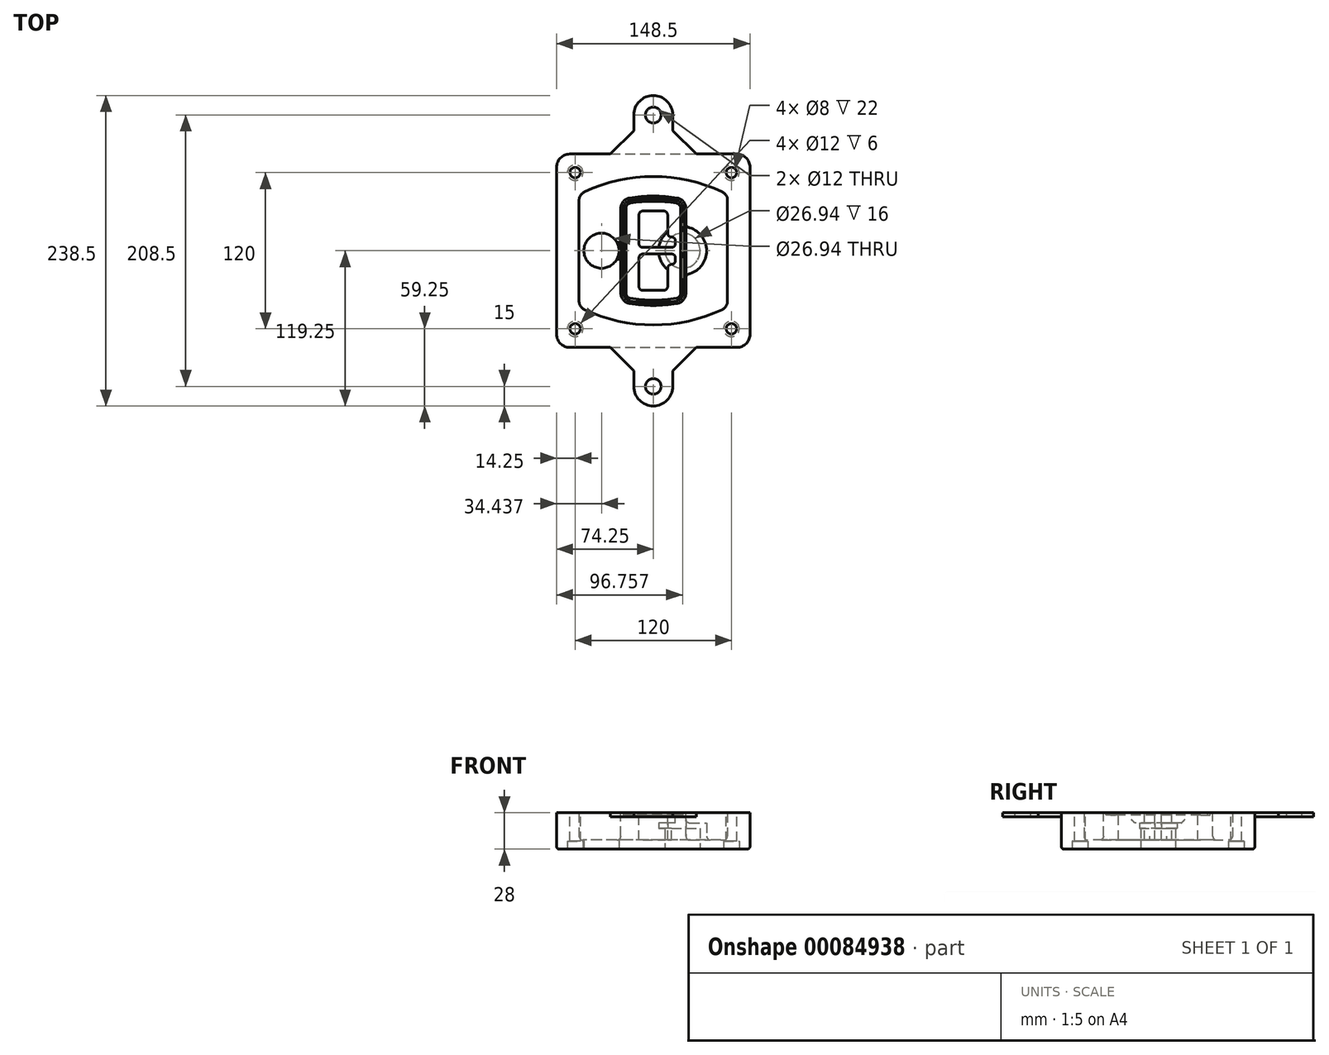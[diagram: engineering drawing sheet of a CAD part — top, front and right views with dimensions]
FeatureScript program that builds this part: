
annotation { "Feature Type Name" : "Feature", "Feature Type Description" : "" }
export const myFeature = defineFeature(function(context is Context, id is Id, definition is map)
    precondition{}
    {
        {
            var Q0;
            Q0=qCreatedBy(makeId("Top.planeOp"),FACE);
            var sketch = newSketch(context, id + "F0", { "sketchPlane" : qUnion([Q0])});
            skPoint(sketch, "E0.rect.middle", {"position": v(0, 0) * mm});
            skLineSegment(sketch, "E1.bottom", {"start": v(-64.25, -74.25) * mm, "end": v(64.25, -74.25) * mm});
            skLineSegment(sketch, "E1.top", {"start": v(-64.25, 74.25) * mm, "end": v(64.25, 74.25) * mm});
            skLineSegment(sketch, "E1.left", {"start": v(-74.25, -64.25) * mm, "end": v(-74.25, 64.25) * mm});
            skLineSegment(sketch, "E1.right", {"start": v(74.25, -64.25) * mm, "end": v(74.25, 64.25) * mm});
            skLineSegment(sketch, "E2", {"start": v(-74.25, 74.25) * mm, "end": v(74.25, -74.25) * mm, "construction": true});
            skLineSegment(sketch, "E3", {"start": v(74.25, 74.25) * mm, "end": v(-74.25, -74.25) * mm, "construction": true});
            skCircle(sketch, "E4", {"center": v(-60, 60) * mm, "radius": 4 * mm});
            skCircle(sketch, "E5", {"center": v(60, 60) * mm, "radius": 4 * mm});
            skCircle(sketch, "E6", {"center": v(60, -60) * mm, "radius": 4 * mm});
            skCircle(sketch, "E7", {"center": v(-60, -60) * mm, "radius": 4 * mm});
            skLineSegment(sketch, "E8", {"start": v(-60, 60) * mm, "end": v(60, 60) * mm, "construction": true});
            skLineSegment(sketch, "E9", {"start": v(60, 60) * mm, "end": v(60, -60) * mm, "construction": true});
            skLineSegment(sketch, "E10", {"start": v(60, -60) * mm, "end": v(-60, -60) * mm, "construction": true});
            skLineSegment(sketch, "E11", {"start": v(-60, -60) * mm, "end": v(-60, 60) * mm, "construction": true});
            skLineSegment(sketch, "E12", {"start": v(-60, 38.83) * mm, "end": v(-60, -38.83) * mm});
            skLineSegment(sketch, "E13", {"start": v(60, 38.83) * mm, "end": v(60, -38.83) * mm});
            skArc(sketch, "E14", {"start": v(54.26, 47.88) * mm, "mid": v(0, 60) * mm, "end": v(-54.26, 47.88) * mm});
            skArc(sketch, "E15", {"start": v(-54.26, -47.88) * mm, "mid": v(0, -60) * mm, "end": v(54.26, -47.88) * mm});
            skLineSegment(sketch, "E16", {"start": v(-60, 0) * mm, "end": v(60, 0) * mm, "construction": true});
            skPoint(sketch, "E17.visualSharp", {"position": v(-60, -45) * mm});
            skArc(sketch, "E17.filletArc", {"start": v(-60, -38.83) * mm, "mid": v(-58.44, -44.2) * mm, "end": v(-54.26, -47.88) * mm});
            skPoint(sketch, "E18.visualSharp", {"position": v(-60, 45) * mm});
            skArc(sketch, "E18.filletArc", {"start": v(-54.26, 47.88) * mm, "mid": v(-58.44, 44.2) * mm, "end": v(-60, 38.83) * mm});
            skPoint(sketch, "E19.visualSharp", {"position": v(60, 45) * mm});
            skArc(sketch, "E19.filletArc", {"start": v(60, 38.83) * mm, "mid": v(58.44, 44.2) * mm, "end": v(54.26, 47.88) * mm});
            skPoint(sketch, "E20.visualSharp", {"position": v(60, -45) * mm});
            skArc(sketch, "E20.filletArc", {"start": v(54.26, -47.88) * mm, "mid": v(58.44, -44.2) * mm, "end": v(60, -38.83) * mm});
            skPoint(sketch, "E21.visualSharp", {"position": v(-74.25, 74.25) * mm});
            skArc(sketch, "E21.filletArc", {"start": v(-64.25, 74.25) * mm, "mid": v(-71.32, 71.32) * mm, "end": v(-74.25, 64.25) * mm});
            skPoint(sketch, "E22.visualSharp", {"position": v(74.25, 74.25) * mm});
            skArc(sketch, "E22.filletArc", {"start": v(74.25, 64.25) * mm, "mid": v(71.32, 71.32) * mm, "end": v(64.25, 74.25) * mm});
            skPoint(sketch, "E23.visualSharp", {"position": v(74.25, -74.25) * mm});
            skArc(sketch, "E23.filletArc", {"start": v(64.25, -74.25) * mm, "mid": v(71.32, -71.32) * mm, "end": v(74.25, -64.25) * mm});
            skPoint(sketch, "E24.visualSharp", {"position": v(-74.25, -74.25) * mm});
            skArc(sketch, "E24.filletArc", {"start": v(-74.25, -64.25) * mm, "mid": v(-71.32, -71.32) * mm, "end": v(-64.25, -74.25) * mm});
            skArc(sketch, "E25.0", {"start": v(57, 38.83) * mm, "mid": v(55.9, 42.58) * mm, "end": v(52.98, 45.17) * mm});
            skLineSegment(sketch, "E25.1", {"start": v(57, 38.83) * mm, "end": v(57, -38.83) * mm});
            skArc(sketch, "E25.2", {"start": v(52.98, -45.17) * mm, "mid": v(55.9, -42.58) * mm, "end": v(57, -38.83) * mm});
            skArc(sketch, "E25.3", {"start": v(-52.98, -45.17) * mm, "mid": v(0, -57) * mm, "end": v(52.98, -45.17) * mm});
            skArc(sketch, "E25.4", {"start": v(-57, -38.83) * mm, "mid": v(-55.9, -42.58) * mm, "end": v(-52.98, -45.17) * mm});
            skArc(sketch, "E25.5", {"start": v(52.98, 45.17) * mm, "mid": v(0, 57) * mm, "end": v(-52.98, 45.17) * mm});
            skLineSegment(sketch, "E25.6", {"start": v(-57, 38.83) * mm, "end": v(-57, -38.83) * mm});
            skArc(sketch, "E25.7", {"start": v(-52.98, 45.17) * mm, "mid": v(-55.9, 42.58) * mm, "end": v(-57, 38.83) * mm});
            skArc(sketch, "E26.0", {"start": v(-55.96, 51.5) * mm, "mid": v(-61.82, 46.33) * mm, "end": v(-64, 38.83) * mm});
            skArc(sketch, "E26.1", {"start": v(55.96, 51.5) * mm, "mid": v(0, 64) * mm, "end": v(-55.96, 51.5) * mm});
            skArc(sketch, "E26.2", {"start": v(64, 38.83) * mm, "mid": v(61.82, 46.33) * mm, "end": v(55.96, 51.5) * mm});
            skLineSegment(sketch, "E26.3", {"start": v(64, 38.83) * mm, "end": v(64, -38.83) * mm});
            skArc(sketch, "E26.4", {"start": v(55.96, -51.5) * mm, "mid": v(61.82, -46.33) * mm, "end": v(64, -38.83) * mm});
            skLineSegment(sketch, "E26.5", {"start": v(-64, 38.83) * mm, "end": v(-64, -38.83) * mm});
            skArc(sketch, "E26.6", {"start": v(-55.96, -51.5) * mm, "mid": v(0, -64) * mm, "end": v(55.96, -51.5) * mm});
            skArc(sketch, "E26.7", {"start": v(-64, -38.83) * mm, "mid": v(-61.82, -46.33) * mm, "end": v(-55.96, -51.5) * mm});
            skSolve(sketch);
        }
        {
            var Q0;
            Q0=makeQuery(id+"F0.imprint","IMPRINT",FACE,{"disambiguationData":[TD([[makeQuery(id+"F0.imprint","IMPRINT",EDGE,{"derivedFrom":sQuery(id+"F0.wireOp",EDGE,"E1.bottom")}),1.0]])]});
            var Q1;
            Q1=makeQuery(id+"F0.imprint","IMPRINT",FACE,{"disambiguationData":[TD([[makeQuery(id+"F0.imprint","IMPRINT",EDGE,{"derivedFrom":sQuery(id+"F0.wireOp",EDGE,"E12")}),1.0]])]});
            var Q2;
            Q2=makeQuery(id+"F0.imprint","IMPRINT",FACE,{"disambiguationData":[TD([[makeQuery(id+"F0.imprint","IMPRINT",EDGE,{"derivedFrom":sQuery(id+"F0.wireOp",EDGE,"E25.0")}),1.0]])]});
            var Q3;
            Q3=makeQuery(id+"F0.imprint","IMPRINT",FACE,{"disambiguationData":[TD([[makeQuery(id+"F0.imprint","IMPRINT",EDGE,{"derivedFrom":sQuery(id+"F0.wireOp",EDGE,"E12")}),-1.0]])]});
            extrude(context, id + "F1", {"entities" : qUnion([Q0, Q1, Q2, Q3]), "oppositeDirection" : true, "depth" : 25 * mm});
        }
        {
            var Q0;
            Q0=makeQuery(id+"F0.imprint","IMPRINT",FACE,{"disambiguationData":[TD([[makeQuery(id+"F0.imprint","IMPRINT",EDGE,{"derivedFrom":sQuery(id+"F0.wireOp",EDGE,"E12")}),1.0]])]});
            extrude(context, id + "F2", {"entities" : qUnion([Q0]), "operationType" : NewBodyOperationType.ADD, "depth" : 3 * mm});
        }
        {
            var Q0;
            Q0=makeQuery(id+"F0.imprint","IMPRINT",FACE,{"disambiguationData":[TD([[makeQuery(id+"F0.imprint","IMPRINT",EDGE,{"derivedFrom":sQuery(id+"F0.wireOp",EDGE,"E25.0")}),1.0]])]});
            extrude(context, id + "F3", {"entities" : qUnion([Q0]), "operationType" : NewBodyOperationType.REMOVE, "oppositeDirection" : true, "depth" : 18 * mm});
        }
        {
            var Q0;
            Q0=makeQuery(id+"F2.opExtrude","CAP_FACE",FACE,{"disambiguationData":[OSD([sQuery(id+"F0.wireOp",EDGE,"E12"),sQuery(id+"F0.wireOp",EDGE,"E13"),sQuery(id+"F0.wireOp",EDGE,"E14"),sQuery(id+"F0.wireOp",EDGE,"E15"),sQuery(id+"F0.wireOp",EDGE,"E17.filletArc"),sQuery(id+"F0.wireOp",EDGE,"E18.filletArc"),sQuery(id+"F0.wireOp",EDGE,"E19.filletArc"),sQuery(id+"F0.wireOp",EDGE,"E20.filletArc"),sQuery(id+"F0.wireOp",EDGE,"E25.0"),sQuery(id+"F0.wireOp",EDGE,"E25.1"),sQuery(id+"F0.wireOp",EDGE,"E25.2"),sQuery(id+"F0.wireOp",EDGE,"E25.3"),sQuery(id+"F0.wireOp",EDGE,"E25.4"),sQuery(id+"F0.wireOp",EDGE,"E25.5"),sQuery(id+"F0.wireOp",EDGE,"E25.6"),sQuery(id+"F0.wireOp",EDGE,"E25.7")])],"isStart":false});
            var sketch = newSketch(context, id + "F4", { "sketchPlane" : qUnion([Q0])});
            skArc(sketch, "E27.0", {"start": v(-18.34, -40.45) * mm, "mid": v(0, -42) * mm, "end": v(18.34, -40.45) * mm});
            skArc(sketch, "E28.0", {"start": v(18.34, 40.45) * mm, "mid": v(0, 42) * mm, "end": v(-18.34, 40.45) * mm});
            skLineSegment(sketch, "E29", {"start": v(-25, 32.57) * mm, "end": v(-25, -32.57) * mm});
            skLineSegment(sketch, "E30", {"start": v(25, 32.57) * mm, "end": v(25, -32.57) * mm});
            skLineSegment(sketch, "E31", {"start": v(-25, 39.1) * mm, "end": v(25, 39.1) * mm, "construction": true});
            skLineSegment(sketch, "E32", {"start": v(-25, -39.1) * mm, "end": v(25, -39.1) * mm, "construction": true});
            skPoint(sketch, "E33.visualSharp", {"position": v(-25, 39.1) * mm});
            skArc(sketch, "E33.filletArc", {"start": v(-18.34, 40.45) * mm, "mid": v(-23.11, 37.73) * mm, "end": v(-25, 32.57) * mm});
            skPoint(sketch, "E34.visualSharp", {"position": v(25, 39.1) * mm});
            skArc(sketch, "E34.filletArc", {"start": v(25, 32.57) * mm, "mid": v(23.11, 37.73) * mm, "end": v(18.34, 40.45) * mm});
            skPoint(sketch, "E35.visualSharp", {"position": v(25, -39.1) * mm});
            skArc(sketch, "E35.filletArc", {"start": v(18.34, -40.45) * mm, "mid": v(23.11, -37.73) * mm, "end": v(25, -32.57) * mm});
            skPoint(sketch, "E36.visualSharp", {"position": v(-25, -39.1) * mm});
            skArc(sketch, "E36.filletArc", {"start": v(-25, -32.57) * mm, "mid": v(-23.11, -37.73) * mm, "end": v(-18.34, -40.45) * mm});
            skArc(sketch, "E37.0", {"start": v(52.98, 45.17) * mm, "mid": v(0, 57) * mm, "end": v(-52.98, 45.17) * mm});
            skArc(sketch, "E37.1", {"start": v(-52.98, 45.17) * mm, "mid": v(-55.9, 42.58) * mm, "end": v(-57, 38.83) * mm});
            skLineSegment(sketch, "E37.2", {"start": v(-57, 38.83) * mm, "end": v(-57, -38.83) * mm});
            skArc(sketch, "E37.3", {"start": v(-57, -38.83) * mm, "mid": v(-55.9, -42.58) * mm, "end": v(-52.98, -45.17) * mm});
            skArc(sketch, "E37.4", {"start": v(-52.98, -45.17) * mm, "mid": v(0, -57) * mm, "end": v(52.98, -45.17) * mm});
            skArc(sketch, "E37.5", {"start": v(52.98, -45.17) * mm, "mid": v(55.9, -42.58) * mm, "end": v(57, -38.83) * mm});
            skLineSegment(sketch, "E37.6", {"start": v(57, 38.83) * mm, "end": v(57, -38.83) * mm});
            skArc(sketch, "E37.7", {"start": v(57, 38.83) * mm, "mid": v(55.9, 42.58) * mm, "end": v(52.98, 45.17) * mm});
            skLineSegment(sketch, "E38.0", {"start": v(23, 32.57) * mm, "end": v(23, -32.57) * mm});
            skArc(sketch, "E38.1", {"start": v(18, -38.48) * mm, "mid": v(21.58, -36.44) * mm, "end": v(23, -32.57) * mm});
            skArc(sketch, "E38.2", {"start": v(-18, -38.48) * mm, "mid": v(0, -40) * mm, "end": v(18, -38.48) * mm});
            skArc(sketch, "E38.3", {"start": v(-23, -32.57) * mm, "mid": v(-21.58, -36.44) * mm, "end": v(-18, -38.48) * mm});
            skLineSegment(sketch, "E38.4", {"start": v(-23, 32.57) * mm, "end": v(-23, -32.57) * mm});
            skArc(sketch, "E38.5", {"start": v(23, 32.57) * mm, "mid": v(21.58, 36.44) * mm, "end": v(18, 38.48) * mm});
            skArc(sketch, "E38.6", {"start": v(-18, 38.48) * mm, "mid": v(-21.58, 36.44) * mm, "end": v(-23, 32.57) * mm});
            skArc(sketch, "E38.7", {"start": v(18, 38.48) * mm, "mid": v(0, 40) * mm, "end": v(-18, 38.48) * mm});
            skArc(sketch, "E39.0", {"start": v(21, 32.57) * mm, "mid": v(20.06, 35.15) * mm, "end": v(17.67, 36.5) * mm});
            skLineSegment(sketch, "E39.1", {"start": v(21, 32.57) * mm, "end": v(21, -32.57) * mm});
            skArc(sketch, "E39.2", {"start": v(17.67, -36.5) * mm, "mid": v(20.06, -35.15) * mm, "end": v(21, -32.57) * mm});
            skArc(sketch, "E39.3", {"start": v(-17.67, -36.5) * mm, "mid": v(0, -38) * mm, "end": v(17.67, -36.5) * mm});
            skArc(sketch, "E39.4", {"start": v(-21, -32.57) * mm, "mid": v(-20.06, -35.15) * mm, "end": v(-17.67, -36.5) * mm});
            skArc(sketch, "E39.5", {"start": v(17.67, 36.5) * mm, "mid": v(0, 38) * mm, "end": v(-17.67, 36.5) * mm});
            skLineSegment(sketch, "E39.6", {"start": v(-21, 32.57) * mm, "end": v(-21, -32.57) * mm});
            skArc(sketch, "E39.7", {"start": v(-17.67, 36.5) * mm, "mid": v(-20.06, 35.15) * mm, "end": v(-21, 32.57) * mm});
            skLineSegment(sketch, "E40", {"start": v(-25, 0) * mm, "end": v(25, 0) * mm, "construction": true});
            skLineSegment(sketch, "E41", {"start": v(-11, 5.5) * mm, "end": v(-11, 27.5) * mm});
            skLineSegment(sketch, "E42", {"start": v(-8, 30.5) * mm, "end": v(8, 30.5) * mm});
            skLineSegment(sketch, "E43", {"start": v(11, 27.5) * mm, "end": v(11, 13.5) * mm});
            skLineSegment(sketch, "E44", {"start": v(14, 10.5) * mm, "end": v(14, 10.5) * mm});
            skLineSegment(sketch, "E45", {"start": v(17, 7.5) * mm, "end": v(17, 5.5) * mm});
            skLineSegment(sketch, "E46", {"start": v(14, 2.5) * mm, "end": v(-8, 2.5) * mm});
            skPoint(sketch, "E47.visualSharp", {"position": v(-11, 30.5) * mm});
            skArc(sketch, "E47.filletArc", {"start": v(-8, 30.5) * mm, "mid": v(-10.12, 29.62) * mm, "end": v(-11, 27.5) * mm});
            skPoint(sketch, "E48.visualSharp", {"position": v(11, 30.5) * mm});
            skArc(sketch, "E48.filletArc", {"start": v(11, 27.5) * mm, "mid": v(10.12, 29.62) * mm, "end": v(8, 30.5) * mm});
            skPoint(sketch, "E49.visualSharp", {"position": v(11, 10.5) * mm});
            skArc(sketch, "E49.filletArc", {"start": v(11, 13.5) * mm, "mid": v(11.88, 11.38) * mm, "end": v(14, 10.5) * mm});
            skPoint(sketch, "E50.visualSharp", {"position": v(17, 10.5) * mm});
            skArc(sketch, "E50.filletArc", {"start": v(17, 7.5) * mm, "mid": v(16.12, 9.62) * mm, "end": v(14, 10.5) * mm});
            skPoint(sketch, "E51.visualSharp", {"position": v(17, 2.5) * mm});
            skArc(sketch, "E51.filletArc", {"start": v(14, 2.5) * mm, "mid": v(16.12, 3.38) * mm, "end": v(17, 5.5) * mm});
            skPoint(sketch, "E52.visualSharp", {"position": v(-11, 2.5) * mm});
            skArc(sketch, "E52.filletArc", {"start": v(-11, 5.5) * mm, "mid": v(-10.12, 3.38) * mm, "end": v(-8, 2.5) * mm});
            skLineSegment(sketch, "E53.0.MirrorCS", {"start": v(14, -2.5) * mm, "end": v(-8, -2.5) * mm});
            skArc(sketch, "E54.0.MirrorCS", {"start": v(-11, -5.5) * mm, "mid": v(-10.12, -3.38) * mm, "end": v(-8, -2.5) * mm});
            skLineSegment(sketch, "E55.0.MirrorCS", {"start": v(-11, -5.5) * mm, "end": v(-11, -27.5) * mm});
            skArc(sketch, "E56.0.MirrorCS", {"start": v(-8, -30.5) * mm, "mid": v(-10.12, -29.62) * mm, "end": v(-11, -27.5) * mm});
            skLineSegment(sketch, "E57.0.MirrorCS", {"start": v(-8, -30.5) * mm, "end": v(8, -30.5) * mm});
            skArc(sketch, "E58.0.MirrorCS", {"start": v(11, -27.5) * mm, "mid": v(10.12, -29.62) * mm, "end": v(8, -30.5) * mm});
            skLineSegment(sketch, "E59.0.MirrorCS", {"start": v(11, -27.5) * mm, "end": v(11, -13.5) * mm});
            skArc(sketch, "E60.0.MirrorCS", {"start": v(11, -13.5) * mm, "mid": v(11.88, -11.38) * mm, "end": v(14, -10.5) * mm});
            skArc(sketch, "E61.0.MirrorCS", {"start": v(17, -7.5) * mm, "mid": v(16.12, -9.62) * mm, "end": v(14, -10.5) * mm});
            skLineSegment(sketch, "E62.0.MirrorCS", {"start": v(17, -7.5) * mm, "end": v(17, -5.5) * mm});
            skArc(sketch, "E63.0.MirrorCS", {"start": v(14, -2.5) * mm, "mid": v(16.12, -3.38) * mm, "end": v(17, -5.5) * mm});
            skSolve(sketch);
        }
        {
            var Q0;
            Q0=makeQuery(id+"F4.imprint","IMPRINT",FACE,{"disambiguationData":[TD([[makeQuery(id+"F4.imprint","IMPRINT",EDGE,{"derivedFrom":sQuery(id+"F4.wireOp",EDGE,"E27.0")}),1.0]])]});
            var Q1;
            Q1=makeQuery(id+"F4.imprint","IMPRINT",FACE,{"disambiguationData":[TD([[makeQuery(id+"F4.imprint","IMPRINT",EDGE,{"derivedFrom":sQuery(id+"F4.wireOp",EDGE,"E38.0")}),-1.0]])]});
            var Q2;
            Q2=makeQuery(id+"F4.imprint","IMPRINT",FACE,{"disambiguationData":[TD([[makeQuery(id+"F4.imprint","IMPRINT",EDGE,{"derivedFrom":sQuery(id+"F4.wireOp",EDGE,"E39.0")}),1.0]])]});
            extrude(context, id + "F5", {"entities" : qUnion([Q0, Q1, Q2]), "operationType" : NewBodyOperationType.ADD, "endBound" : BoundingType.UP_TO_NEXT, "oppositeDirection" : true, "depth" : 25 * mm});
        }
        {
            var Q0;
            Q0=makeQuery(id+"F4.imprint","IMPRINT",FACE,{"disambiguationData":[TD([[makeQuery(id+"F4.imprint","IMPRINT",EDGE,{"derivedFrom":sQuery(id+"F4.wireOp",EDGE,"E38.0")}),-1.0]])]});
            extrude(context, id + "F6", {"entities" : qUnion([Q0]), "operationType" : NewBodyOperationType.REMOVE, "oppositeDirection" : true, "depth" : 2 * mm});
        }
        {
            var Q0;
            Q0=makeQuery(id+"F1.opExtrude","CAP_FACE",FACE,{"disambiguationData":[OSD([sQuery(id+"F0.wireOp",EDGE,"E1.bottom"),sQuery(id+"F0.wireOp",EDGE,"E1.top"),sQuery(id+"F0.wireOp",EDGE,"E1.left"),sQuery(id+"F0.wireOp",EDGE,"E1.right"),sQuery(id+"F0.wireOp",EDGE,"E4"),sQuery(id+"F0.wireOp",EDGE,"E5"),sQuery(id+"F0.wireOp",EDGE,"E6"),sQuery(id+"F0.wireOp",EDGE,"E7"),sQuery(id+"F0.wireOp",EDGE,"E21.filletArc"),sQuery(id+"F0.wireOp",EDGE,"E22.filletArc"),sQuery(id+"F0.wireOp",EDGE,"E23.filletArc"),sQuery(id+"F0.wireOp",EDGE,"E24.filletArc")])],"isStart":false});
            var sketch = newSketch(context, id + "F7", { "sketchPlane" : qUnion([Q0])});
            skCircle(sketch, "E64", {"center": v(22.5, 0) * mm, "radius": 13.47 * mm});
            skCircle(sketch, "E65", {"center": v(-39.81, 0) * mm, "radius": 13.47 * mm});
            skLineSegment(sketch, "E66", {"start": v(74.25, 0) * mm, "end": v(-74.25, 0) * mm});
            skCircle(sketch, "E67", {"center": v(22.5, 0) * mm, "radius": 18.47 * mm});
            skCircle(sketch, "E68", {"center": v(60, -60) * mm, "radius": 6 * mm});
            skCircle(sketch, "E69", {"center": v(-60, -60) * mm, "radius": 6 * mm});
            skCircle(sketch, "E70", {"center": v(-60, 60) * mm, "radius": 6 * mm});
            skCircle(sketch, "E71", {"center": v(60, 60) * mm, "radius": 6 * mm});
            skSolve(sketch);
        }
        {
            var Q0;
            {var subQ1=sQuery(id+"F7.wireOp",EDGE,"E66");var subQ4=sQuery(id+"F7.wireOp",EDGE,"E64");var subQ6=makeQuery(id+"F7.imprint","INTERSECT",VERTEX,{"disambiguationData":[OD(0.0)],"derivedFrom":[subQ4,subQ1]});Q0=makeQuery(id+"F7.imprint","IMPRINT",FACE,{"disambiguationData":[TD([[makeQuery(id+"F7.imprint","IMPRINT",EDGE,{"disambiguationData":[TD([[subQ6,-1.0]])],"derivedFrom":subQ4}),-1.0]])]});}
            var Q1;
            {var subQ0=sQuery(id+"F7.wireOp",EDGE,"E66");var subQ1=sQuery(id+"F7.wireOp",EDGE,"E64");var subQ3=makeQuery(id+"F7.imprint","INTERSECT",VERTEX,{"disambiguationData":[OD(0.0)],"derivedFrom":[subQ1,subQ0]});Q1=makeQuery(id+"F7.imprint","IMPRINT",FACE,{"disambiguationData":[TD([[makeQuery(id+"F7.imprint","IMPRINT",EDGE,{"disambiguationData":[TD([[subQ3,-1.0]])],"derivedFrom":subQ1}),1.0]])]});}
            var Q2;
            {var subQ0=sQuery(id+"F7.wireOp",EDGE,"E66");var subQ1=sQuery(id+"F7.wireOp",EDGE,"E64");var subQ3=makeQuery(id+"F7.imprint","INTERSECT",VERTEX,{"disambiguationData":[OD(0.0)],"derivedFrom":[subQ1,subQ0]});Q2=makeQuery(id+"F7.imprint","IMPRINT",FACE,{"disambiguationData":[TD([[makeQuery(id+"F7.imprint","IMPRINT",EDGE,{"disambiguationData":[TD([[subQ3,1.0]])],"derivedFrom":subQ1}),1.0]])]});}
            var Q3;
            {var subQ1=sQuery(id+"F7.wireOp",EDGE,"E66");var subQ4=sQuery(id+"F7.wireOp",EDGE,"E64");var subQ6=makeQuery(id+"F7.imprint","INTERSECT",VERTEX,{"disambiguationData":[OD(0.0)],"derivedFrom":[subQ4,subQ1]});Q3=makeQuery(id+"F7.imprint","IMPRINT",FACE,{"disambiguationData":[TD([[makeQuery(id+"F7.imprint","IMPRINT",EDGE,{"disambiguationData":[TD([[subQ6,1.0]])],"derivedFrom":subQ4}),-1.0]])]});}
            extrude(context, id + "F8", {"entities" : qUnion([Q0, Q1, Q2, Q3]), "operationType" : NewBodyOperationType.ADD, "oppositeDirection" : true, "depth" : 20 * mm});
        }
        {
            var Q0;
            {var subQ0=sQuery(id+"F7.wireOp",EDGE,"E66");var subQ1=sQuery(id+"F7.wireOp",EDGE,"E64");var subQ3=makeQuery(id+"F7.imprint","INTERSECT",VERTEX,{"disambiguationData":[OD(0.0)],"derivedFrom":[subQ1,subQ0]});Q0=makeQuery(id+"F7.imprint","IMPRINT",FACE,{"disambiguationData":[TD([[makeQuery(id+"F7.imprint","IMPRINT",EDGE,{"disambiguationData":[TD([[subQ3,-1.0]])],"derivedFrom":subQ1}),1.0]])]});}
            var Q1;
            {var subQ0=sQuery(id+"F7.wireOp",EDGE,"E66");var subQ1=sQuery(id+"F7.wireOp",EDGE,"E64");var subQ3=makeQuery(id+"F7.imprint","INTERSECT",VERTEX,{"disambiguationData":[OD(0.0)],"derivedFrom":[subQ1,subQ0]});Q1=makeQuery(id+"F7.imprint","IMPRINT",FACE,{"disambiguationData":[TD([[makeQuery(id+"F7.imprint","IMPRINT",EDGE,{"disambiguationData":[TD([[subQ3,1.0]])],"derivedFrom":subQ1}),1.0]])]});}
            extrude(context, id + "F9", {"entities" : qUnion([Q0, Q1]), "operationType" : NewBodyOperationType.REMOVE, "oppositeDirection" : true, "depth" : 16 * mm});
        }
        {
            var Q0;
            {var subQ0=sQuery(id+"F7.wireOp",EDGE,"E66");var subQ1=sQuery(id+"F7.wireOp",EDGE,"E65");var subQ3=makeQuery(id+"F7.imprint","INTERSECT",VERTEX,{"disambiguationData":[OD(0.0)],"derivedFrom":[subQ1,subQ0]});Q0=makeQuery(id+"F7.imprint","IMPRINT",FACE,{"disambiguationData":[TD([[makeQuery(id+"F7.imprint","IMPRINT",EDGE,{"disambiguationData":[TD([[subQ3,-1.0]])],"derivedFrom":subQ1}),1.0]])]});}
            var Q1;
            {var subQ0=sQuery(id+"F7.wireOp",EDGE,"E66");var subQ1=sQuery(id+"F7.wireOp",EDGE,"E65");var subQ3=makeQuery(id+"F7.imprint","INTERSECT",VERTEX,{"disambiguationData":[OD(0.0)],"derivedFrom":[subQ1,subQ0]});Q1=makeQuery(id+"F7.imprint","IMPRINT",FACE,{"disambiguationData":[TD([[makeQuery(id+"F7.imprint","IMPRINT",EDGE,{"disambiguationData":[TD([[subQ3,1.0]])],"derivedFrom":subQ1}),1.0]])]});}
            extrude(context, id + "F10", {"entities" : qUnion([Q0, Q1]), "operationType" : NewBodyOperationType.REMOVE, "oppositeDirection" : true, "depth" : 25 * mm});
        }
        {
            var Q0;
            Q0=makeQuery(id+"F7.imprint","IMPRINT",FACE,{"disambiguationData":[TD([[makeQuery(id+"F7.imprint","IMPRINT",EDGE,{"derivedFrom":sQuery(id+"F7.wireOp",EDGE,"E68")}),1.0]])]});
            var Q1;
            Q1=makeQuery(id+"F7.imprint","IMPRINT",FACE,{"disambiguationData":[TD([[makeQuery(id+"F7.imprint","IMPRINT",EDGE,{"derivedFrom":makeQuery(id+"F1.opExtrude","CAP_EDGE",EDGE,{"disambiguationData":[OSD([sQuery(id+"F0.wireOp",EDGE,"E5")])],"isStart":false})}),-1.0]])]});
            var Q2;
            Q2=makeQuery(id+"F7.imprint","IMPRINT",FACE,{"disambiguationData":[TD([[makeQuery(id+"F7.imprint","IMPRINT",EDGE,{"derivedFrom":sQuery(id+"F7.wireOp",EDGE,"E69")}),1.0]])]});
            var Q3;
            Q3=makeQuery(id+"F7.imprint","IMPRINT",FACE,{"disambiguationData":[TD([[makeQuery(id+"F7.imprint","IMPRINT",EDGE,{"derivedFrom":makeQuery(id+"F1.opExtrude","CAP_EDGE",EDGE,{"disambiguationData":[OSD([sQuery(id+"F0.wireOp",EDGE,"E4")])],"isStart":false})}),-1.0]])]});
            var Q4;
            Q4=makeQuery(id+"F7.imprint","IMPRINT",FACE,{"disambiguationData":[TD([[makeQuery(id+"F7.imprint","IMPRINT",EDGE,{"derivedFrom":sQuery(id+"F7.wireOp",EDGE,"E70")}),1.0]])]});
            var Q5;
            Q5=makeQuery(id+"F7.imprint","IMPRINT",FACE,{"disambiguationData":[TD([[makeQuery(id+"F7.imprint","IMPRINT",EDGE,{"derivedFrom":makeQuery(id+"F1.opExtrude","CAP_EDGE",EDGE,{"disambiguationData":[OSD([sQuery(id+"F0.wireOp",EDGE,"E7")])],"isStart":false})}),-1.0]])]});
            var Q6;
            Q6=makeQuery(id+"F7.imprint","IMPRINT",FACE,{"disambiguationData":[TD([[makeQuery(id+"F7.imprint","IMPRINT",EDGE,{"derivedFrom":sQuery(id+"F7.wireOp",EDGE,"E71")}),1.0]])]});
            var Q7;
            Q7=makeQuery(id+"F7.imprint","IMPRINT",FACE,{"disambiguationData":[TD([[makeQuery(id+"F7.imprint","IMPRINT",EDGE,{"derivedFrom":makeQuery(id+"F1.opExtrude","CAP_EDGE",EDGE,{"disambiguationData":[OSD([sQuery(id+"F0.wireOp",EDGE,"E6")])],"isStart":false})}),-1.0]])]});
            extrude(context, id + "F11", {"entities" : qUnion([Q0, Q1, Q2, Q3, Q4, Q5, Q6, Q7]), "operationType" : NewBodyOperationType.REMOVE, "oppositeDirection" : true, "depth" : 6 * mm});
        }
        {
            var Q0;
            Q0=makeQuery(id+"F9.boolean.opBoolean","COPY",FACE,{"derivedFrom":makeQuery(id+"F9.opExtrude","CAP_FACE",FACE,{"disambiguationData":[OSD([sQuery(id+"F7.wireOp",EDGE,"E64")])],"isStart":false})});
            var sketch = newSketch(context, id + "F12", { "sketchPlane" : qUnion([Q0])});
            skArc(sketch, "E72.0", {"start": v(11, 14.45) * mm, "mid": v(6.45, 9.13) * mm, "end": v(4.2, 2.5) * mm});
            skArc(sketch, "E72.1", {"start": v(4.2, -2.5) * mm, "mid": v(6.45, -9.13) * mm, "end": v(11, -14.45) * mm});
            skLineSegment(sketch, "E73", {"start": v(4.2, -2.5) * mm, "end": v(14, -2.5) * mm});
            skLineSegment(sketch, "E74.0", {"start": v(14, 2.5) * mm, "end": v(4.2, 2.5) * mm});
            skArc(sketch, "E74.1", {"start": v(14, 2.5) * mm, "mid": v(16.12, 3.38) * mm, "end": v(17, 5.5) * mm});
            skLineSegment(sketch, "E74.2", {"start": v(17, 7.5) * mm, "end": v(17, 5.5) * mm});
            skArc(sketch, "E74.3", {"start": v(17, 7.5) * mm, "mid": v(16.12, 9.62) * mm, "end": v(14, 10.5) * mm});
            skArc(sketch, "E74.4", {"start": v(11, 13.5) * mm, "mid": v(11.88, 11.38) * mm, "end": v(14, 10.5) * mm});
            skLineSegment(sketch, "E74.5", {"start": v(11, 14.45) * mm, "end": v(11, 13.5) * mm});
            skLineSegment(sketch, "E74.7", {"start": v(14, -2.5) * mm, "end": v(4.2, -2.5) * mm});
            skArc(sketch, "E74.8", {"start": v(14, -2.5) * mm, "mid": v(16.12, -3.38) * mm, "end": v(17, -5.5) * mm});
            skLineSegment(sketch, "E74.9", {"start": v(17, -7.5) * mm, "end": v(17, -5.5) * mm});
            skArc(sketch, "E74.10", {"start": v(17, -7.5) * mm, "mid": v(16.12, -9.62) * mm, "end": v(14, -10.5) * mm});
            skArc(sketch, "E74.11", {"start": v(11, -13.5) * mm, "mid": v(11.88, -11.38) * mm, "end": v(14, -10.5) * mm});
            skLineSegment(sketch, "E74.12", {"start": v(11, -14.45) * mm, "end": v(11, -13.5) * mm});
            skPoint(sketch, "E75.orphan", {"position": v(11, -27.5) * mm});
            skPoint(sketch, "E76.orphan", {"position": v(-8, -2.5) * mm});
            skPoint(sketch, "E77.orphan", {"position": v(-8, 2.5) * mm});
            skPoint(sketch, "E78.orphan", {"position": v(11, 27.5) * mm});
            skSolve(sketch);
        }
        {
            var Q0;
            {var subQ7=sQuery(id+"F12.wireOp",EDGE,"E72.0");var subQ14=sQuery(id+"F12.wireOp",EDGE,"E72.1");var subQ16=sQuery(id+"F12.wireOp",EDGE,"E74.1");var subQ18=sQuery(id+"F12.wireOp",EDGE,"E74.8");Q0=qUnion([makeQuery(id+"F12.imprint","IMPRINT",FACE,{"disambiguationData":[TD([[makeQuery(id+"F12.imprint","IMPRINT",EDGE,{"derivedFrom":subQ7}),1.0]])]}),makeQuery(id+"F12.imprint","IMPRINT",FACE,{"disambiguationData":[TD([[makeQuery(id+"F12.imprint","IMPRINT",EDGE,{"derivedFrom":subQ14}),1.0]])]}),makeQuery(id+"F12.imprint","IMPRINT",FACE,{"disambiguationData":[TD([[makeQuery(id+"F12.imprint","IMPRINT",EDGE,{"derivedFrom":subQ16}),1.0]])]}),makeQuery(id+"F12.imprint","IMPRINT",FACE,{"disambiguationData":[TD([[makeQuery(id+"F12.imprint","IMPRINT",EDGE,{"derivedFrom":subQ18}),-1.0]])]})]);}
            var Q1;
            Q1=makeQuery(id+"F5.boolean.opBoolean","SPLIT",FACE,{"disambiguationData":[TD([makeQuery(id+"F5.opExtrude","SWEPT_FACE",FACE,{"disambiguationData":[OSD([sQuery(id+"F4.wireOp",EDGE,"E41")])]})])],"derivedFrom":makeQuery(id+"F3.boolean.opBoolean","COPY",FACE,{"derivedFrom":makeQuery(id+"F3.opExtrude","CAP_FACE",FACE,{"disambiguationData":[OSD([sQuery(id+"F0.wireOp",EDGE,"E25.0"),sQuery(id+"F0.wireOp",EDGE,"E25.1"),sQuery(id+"F0.wireOp",EDGE,"E25.2"),sQuery(id+"F0.wireOp",EDGE,"E25.3"),sQuery(id+"F0.wireOp",EDGE,"E25.4"),sQuery(id+"F0.wireOp",EDGE,"E25.5"),sQuery(id+"F0.wireOp",EDGE,"E25.6"),sQuery(id+"F0.wireOp",EDGE,"E25.7")])],"isStart":false})})});
            extrude(context, id + "F13", {"entities" : qUnion([Q0]), "operationType" : NewBodyOperationType.REMOVE, "endBound" : BoundingType.UP_TO_SURFACE, "endBoundEntityFace" : qUnion([Q1]), "depth" : 25 * mm});
        }
        {
            var Q0;
            Q0=makeQuery(id+"F3.boolean.opBoolean","COPY",EDGE,{"derivedFrom":makeQuery(id+"F3.opExtrude","CAP_EDGE",EDGE,{"disambiguationData":[OSD([sQuery(id+"F0.wireOp",EDGE,"E25.6")])],"isStart":false})});
            var Q1;
            Q1=makeQuery(id+"F8.boolean.opBoolean","INTERSECT",EDGE,{"derivedFrom":[makeQuery(id+"F5.opExtrude","SWEPT_FACE",FACE,{"disambiguationData":[OSD([sQuery(id+"F4.wireOp",EDGE,"E30")])]}),makeQuery(id+"F8.opExtrude","CAP_FACE",FACE,{"disambiguationData":[OSD([sQuery(id+"F7.wireOp",EDGE,"E67")])],"isStart":false})]});
            var Q2;
            Q2=makeQuery(id+"F8.boolean.opBoolean","INTERSECT",EDGE,{"disambiguationData":[OD(1.0)],"derivedFrom":[makeQuery(id+"F5.opExtrude","SWEPT_FACE",FACE,{"disambiguationData":[OSD([sQuery(id+"F4.wireOp",EDGE,"E30")])]}),makeQuery(id+"F8.opExtrude","SWEPT_FACE",FACE,{"disambiguationData":[OSD([sQuery(id+"F7.wireOp",EDGE,"E67")])]})]});
            var Q3;
            {var subQ0=sQuery(id+"F4.wireOp",EDGE,"E30");Q3=makeQuery(id+"F8.boolean.opBoolean","SPLIT",EDGE,{"disambiguationData":[TD([makeQuery(id+"F5.opExtrude","SWEPT_FACE",FACE,{"disambiguationData":[OSD([sQuery(id+"F4.wireOp",EDGE,"E35.filletArc")])]})])],"derivedFrom":makeQuery(id+"F5.opExtrude","CAP_EDGE",EDGE,{"disambiguationData":[OSD([subQ0])],"isStart":false})});}
            var Q4;
            {var subQ0=sQuery(id+"F0.wireOp",EDGE,"E25.7");var subQ1=sQuery(id+"F0.wireOp",EDGE,"E25.1");var subQ2=sQuery(id+"F0.wireOp",EDGE,"E25.6");var subQ3=sQuery(id+"F0.wireOp",EDGE,"E25.5");var subQ4=sQuery(id+"F0.wireOp",EDGE,"E25.4");var subQ5=sQuery(id+"F0.wireOp",EDGE,"E25.0");var subQ6=sQuery(id+"F0.wireOp",EDGE,"E25.2");var subQ7=sQuery(id+"F0.wireOp",EDGE,"E25.3");Q4=makeQuery(id+"F8.boolean.opBoolean","INTERSECT",EDGE,{"derivedFrom":[makeQuery(id+"F5.boolean.opBoolean","SPLIT",FACE,{"disambiguationData":[TD([makeQuery(id+"F2.opExtrude","SWEPT_FACE",FACE,{"disambiguationData":[OSD([subQ5])]})])],"derivedFrom":makeQuery(id+"F3.boolean.opBoolean","COPY",FACE,{"derivedFrom":makeQuery(id+"F3.opExtrude","CAP_FACE",FACE,{"disambiguationData":[OSD([subQ5,subQ1,subQ6,subQ7,subQ4,subQ3,subQ2,subQ0])],"isStart":false})})}),makeQuery(id+"F8.opExtrude","SWEPT_FACE",FACE,{"disambiguationData":[OSD([sQuery(id+"F7.wireOp",EDGE,"E67")])]})]});}
            var Q5;
            Q5=makeQuery(id+"F8.boolean.opBoolean","INTERSECT",EDGE,{"disambiguationData":[OD(0.0)],"derivedFrom":[makeQuery(id+"F5.opExtrude","SWEPT_FACE",FACE,{"disambiguationData":[OSD([sQuery(id+"F4.wireOp",EDGE,"E30")])]}),makeQuery(id+"F8.opExtrude","SWEPT_FACE",FACE,{"disambiguationData":[OSD([sQuery(id+"F7.wireOp",EDGE,"E67")])]})]});
            fillet(context, id + "F14", {"entities" : qUnion([Q0, Q1, Q2, Q3, Q4, Q5]), "radius" : 3 * mm, "tangentPropagation" : true, "allowEdgeOverflow" : false});
        }
        {
            var Q0;
            Q0=makeQuery(id+"F1.opExtrude","CAP_EDGE",EDGE,{"disambiguationData":[OSD([sQuery(id+"F0.wireOp",EDGE,"E1.bottom")])],"isStart":false});
            fillet(context, id + "F15", {"entities" : qUnion([Q0]), "radius" : 2 * mm, "tangentPropagation" : true, "allowEdgeOverflow" : false});
        }
        {
            var Q0;
            {var subQ0=sQuery(id+"F0.wireOp",EDGE,"E22.filletArc");var subQ1=sQuery(id+"F0.wireOp",EDGE,"E7");var subQ2=sQuery(id+"F0.wireOp",EDGE,"E6");var subQ3=sQuery(id+"F0.wireOp",EDGE,"E5");var subQ4=sQuery(id+"F0.wireOp",EDGE,"E4");var subQ5=sQuery(id+"F0.wireOp",EDGE,"E1.bottom");var subQ6=sQuery(id+"F0.wireOp",EDGE,"E21.filletArc");var subQ7=sQuery(id+"F0.wireOp",EDGE,"E1.top");var subQ8=sQuery(id+"F0.wireOp",EDGE,"E1.left");var subQ9=sQuery(id+"F0.wireOp",EDGE,"E1.right");var subQ10=sQuery(id+"F0.wireOp",EDGE,"E23.filletArc");var subQ11=sQuery(id+"F0.wireOp",EDGE,"E24.filletArc");Q0=makeQuery(id+"F2.boolean.opBoolean","SPLIT",FACE,{"disambiguationData":[TD([makeQuery(id+"F1.opExtrude","SWEPT_FACE",FACE,{"disambiguationData":[OSD([subQ5])]})])],"derivedFrom":makeQuery(id+"F1.opExtrude","CAP_FACE",FACE,{"disambiguationData":[OSD([subQ5,subQ7,subQ8,subQ9,subQ4,subQ3,subQ2,subQ1,subQ6,subQ0,subQ10,subQ11])],"isStart":true})});}
            var sketch = newSketch(context, id + "F16", { "sketchPlane" : qUnion([Q0])});
            skCircle(sketch, "E79", {"center": v(0, 104.25) * mm, "radius": 6 * mm});
            skArc(sketch, "E80", {"start": v(-15, 104.25) * mm, "mid": v(0, 119.25) * mm, "end": v(15, 104.25) * mm});
            skLineSegment(sketch, "E81", {"start": v(-15, 104.25) * mm, "end": v(-15, 92.25) * mm});
            skLineSegment(sketch, "E82", {"start": v(15, 104.25) * mm, "end": v(15, 92.25) * mm});
            skLineSegment(sketch, "E83", {"start": v(-15, 92.25) * mm, "end": v(-33, 74.25) * mm});
            skLineSegment(sketch, "E84", {"start": v(15, 92.25) * mm, "end": v(33, 74.25) * mm});
            skLineSegment(sketch, "E85.MirrorCS", {"start": v(-15, -92.25) * mm, "end": v(-33, -74.25) * mm});
            skLineSegment(sketch, "E86.MirrorCS", {"start": v(-15, -104.25) * mm, "end": v(-15, -92.25) * mm});
            skArc(sketch, "E87.MirrorCS", {"start": v(-15, -104.25) * mm, "mid": v(0, -119.25) * mm, "end": v(15, -104.25) * mm});
            skLineSegment(sketch, "E88.MirrorCS", {"start": v(15, -104.25) * mm, "end": v(15, -92.25) * mm});
            skLineSegment(sketch, "E89.MirrorCS", {"start": v(15, -92.25) * mm, "end": v(33, -74.25) * mm});
            skCircle(sketch, "E90.MirrorC", {"center": v(0, -104.25) * mm, "radius": 6 * mm});
            skSolve(sketch);
        }
        {
            var Q0;
            Q0=makeQuery(id+"F16.imprint","IMPRINT",FACE,{"disambiguationData":[TD([[makeQuery(id+"F16.imprint","IMPRINT",EDGE,{"derivedFrom":sQuery(id+"F16.wireOp",EDGE,"E79")}),-1.0]])]});
            var Q1;
            Q1=makeQuery(id+"F16.imprint","IMPRINT",FACE,{"disambiguationData":[TD([[makeQuery(id+"F16.imprint","IMPRINT",EDGE,{"derivedFrom":makeQuery(id+"F1.opExtrude","CAP_EDGE",EDGE,{"disambiguationData":[OSD([sQuery(id+"F0.wireOp",EDGE,"E1.left")])],"isStart":true})}),-1.0]])]});
            var Q2;
            {var subQ0=sQuery(id+"F16.wireOp",EDGE,"E85.MirrorCS");Q2=makeQuery(id+"F16.imprint","IMPRINT",FACE,{"disambiguationData":[TD([[makeQuery(id+"F16.imprint","IMPRINT",EDGE,{"derivedFrom":subQ0}),-1.0]])]});}
            var Q3;
            Q3=makeQuery(id+"F2.opExtrude","CAP_FACE",FACE,{"disambiguationData":[OSD([sQuery(id+"F0.wireOp",EDGE,"E12"),sQuery(id+"F0.wireOp",EDGE,"E13"),sQuery(id+"F0.wireOp",EDGE,"E14"),sQuery(id+"F0.wireOp",EDGE,"E15"),sQuery(id+"F0.wireOp",EDGE,"E17.filletArc"),sQuery(id+"F0.wireOp",EDGE,"E18.filletArc"),sQuery(id+"F0.wireOp",EDGE,"E19.filletArc"),sQuery(id+"F0.wireOp",EDGE,"E20.filletArc"),sQuery(id+"F0.wireOp",EDGE,"E25.0"),sQuery(id+"F0.wireOp",EDGE,"E25.1"),sQuery(id+"F0.wireOp",EDGE,"E25.2"),sQuery(id+"F0.wireOp",EDGE,"E25.3"),sQuery(id+"F0.wireOp",EDGE,"E25.4"),sQuery(id+"F0.wireOp",EDGE,"E25.5"),sQuery(id+"F0.wireOp",EDGE,"E25.6"),sQuery(id+"F0.wireOp",EDGE,"E25.7")])],"isStart":false});
            extrude(context, id + "F17", {"entities" : qUnion([Q0, Q1, Q2]), "operationType" : NewBodyOperationType.ADD, "endBound" : BoundingType.UP_TO_SURFACE, "endBoundEntityFace" : qUnion([Q3]), "depth" : 25 * mm});
        }
    });
